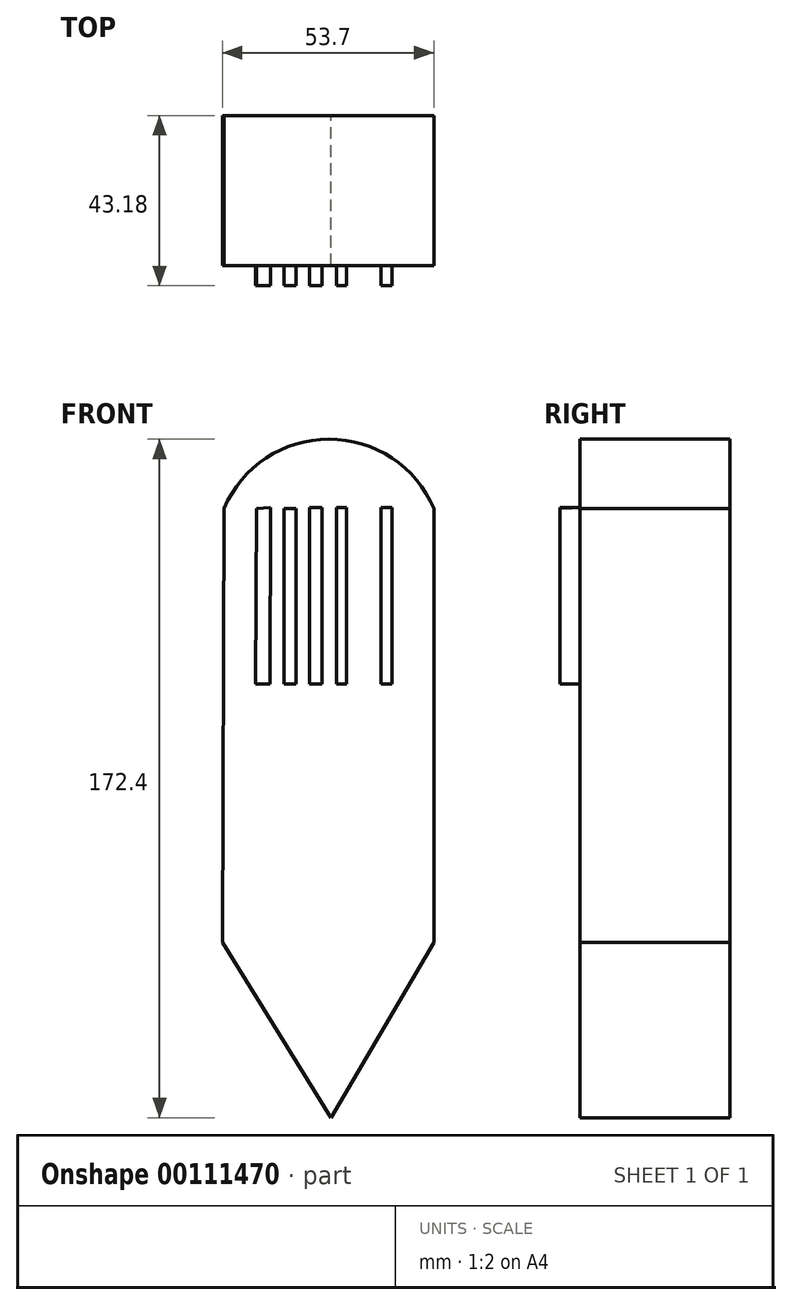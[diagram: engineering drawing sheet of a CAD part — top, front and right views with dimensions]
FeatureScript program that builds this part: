
annotation { "Feature Type Name" : "Feature", "Feature Type Description" : "" }
export const myFeature = defineFeature(function(context is Context, id is Id, definition is map)
    precondition{}
    {
        {
            var Q0;
            Q0=qCreatedBy(makeId("Front.planeOp"),FACE);
            var sketch = newSketch(context, id + "F0", { "sketchPlane" : qUnion([Q0])});
            skLineSegment(sketch, "E0", {"start": v(-36.35, 44.66) * mm, "end": v(-36.76, -65.64) * mm});
            skLineSegment(sketch, "E1", {"start": v(16.94, 44.66) * mm, "end": v(16.94, -65.64) * mm});
            skLineSegment(sketch, "E2", {"start": v(-36.35, 44.66) * mm, "end": v(16.94, 44.66) * mm});
            skArc(sketch, "E3", {"start": v(16.94, 44.66) * mm, "mid": v(-9.7, 62.25) * mm, "end": v(-36.35, 44.66) * mm});
            skLineSegment(sketch, "E4", {"start": v(-36.76, -65.64) * mm, "end": v(-9.16, -110.15) * mm});
            skLineSegment(sketch, "E5", {"start": v(-9.16, -110.15) * mm, "end": v(16.94, -65.64) * mm});
            skLineSegment(sketch, "E6", {"start": v(-17.26, -97.1) * mm, "end": v(-1.5, -97.1) * mm});
            skSolve(sketch);
        }
        {
            var Q0;
            Q0 = qSketchRegion(id + "F0", true);
            extrude(context, id + "F1", {"entities" : qUnion([Q0]), "depth" : 38.1 * mm});
        }
        {
            var Q0;
            Q0=makeQuery(id+"F1.opExtrude","CAP_FACE",FACE,{"disambiguationData":[OSD([sQuery(id+"F0.wireOp",EDGE,"E0"),sQuery(id+"F0.wireOp",EDGE,"E1"),sQuery(id+"F0.wireOp",EDGE,"E3"),sQuery(id+"F0.wireOp",EDGE,"E4"),sQuery(id+"F0.wireOp",EDGE,"E5")])],"isStart":false});
            var sketch = newSketch(context, id + "F2", { "sketchPlane" : qUnion([Q0])});
            skLineSegment(sketch, "E7", {"start": v(-28.14, 44.64) * mm, "end": v(-28.3, 0) * mm});
            skLineSegment(sketch, "E8", {"start": v(-28.3, 0) * mm, "end": v(-24.72, -0.01) * mm});
            skLineSegment(sketch, "E9", {"start": v(-24.72, -0.01) * mm, "end": v(-24.55, 44.84) * mm});
            skLineSegment(sketch, "E10", {"start": v(-24.55, 44.84) * mm, "end": v(-28.14, 44.64) * mm});
            skLineSegment(sketch, "E11", {"start": v(-21.1, 0) * mm, "end": v(-21.1, 44.64) * mm});
            skLineSegment(sketch, "E12", {"start": v(-21.1, 44.64) * mm, "end": v(-18.07, 44.64) * mm});
            skLineSegment(sketch, "E13", {"start": v(-18.07, 44.64) * mm, "end": v(-18.07, 0) * mm});
            skLineSegment(sketch, "E14", {"start": v(-18.07, 0) * mm, "end": v(-21.1, 0) * mm});
            skLineSegment(sketch, "E15", {"start": v(-14.65, 0) * mm, "end": v(-14.65, 44.84) * mm});
            skLineSegment(sketch, "E16", {"start": v(-14.65, 44.84) * mm, "end": v(-11.43, 44.84) * mm});
            skLineSegment(sketch, "E17", {"start": v(-11.43, 44.84) * mm, "end": v(-11.43, 0) * mm});
            skLineSegment(sketch, "E18", {"start": v(-11.43, 0) * mm, "end": v(-14.65, 0) * mm});
            skLineSegment(sketch, "E19", {"start": v(-7.8, 44.84) * mm, "end": v(-7.8, 0) * mm});
            skLineSegment(sketch, "E20", {"start": v(-7.8, 0) * mm, "end": v(-5.18, 0) * mm});
            skLineSegment(sketch, "E21", {"start": v(-5.18, 0) * mm, "end": v(-5.18, 44.84) * mm});
            skLineSegment(sketch, "E22", {"start": v(-5.18, 44.84) * mm, "end": v(-7.8, 44.84) * mm});
            skLineSegment(sketch, "E23", {"start": v(3.48, 44.84) * mm, "end": v(3.48, 0) * mm});
            skLineSegment(sketch, "E24", {"start": v(3.48, 0) * mm, "end": v(6.3, 0) * mm});
            skLineSegment(sketch, "E25", {"start": v(6.3, 0) * mm, "end": v(6.3, 44.84) * mm});
            skLineSegment(sketch, "E26", {"start": v(6.3, 44.84) * mm, "end": v(3.48, 44.84) * mm});
            skSolve(sketch);
        }
        {
            var Q0;
            Q0 = qSketchRegion(id + "F2", true);
            extrude(context, id + "F3", {"entities" : qUnion([Q0]), "operationType" : NewBodyOperationType.ADD, "depth" : 5.08 * mm});
        }
    });
